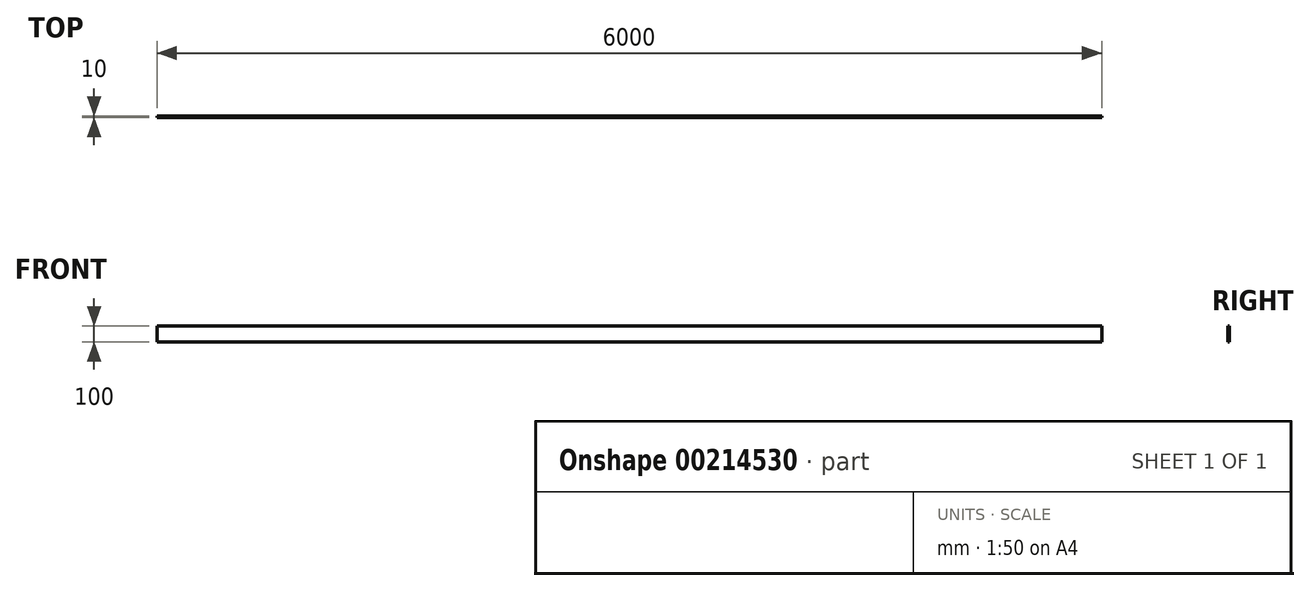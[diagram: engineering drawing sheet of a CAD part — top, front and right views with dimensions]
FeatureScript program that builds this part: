
annotation { "Feature Type Name" : "Feature", "Feature Type Description" : "" }
export const myFeature = defineFeature(function(context is Context, id is Id, definition is map)
    precondition{}
    {
        {
            var Q0;
            Q0=qCreatedBy(makeId("Front.planeOp"),FACE);
            var sketch = newSketch(context, id + "F0", { "sketchPlane" : qUnion([Q0])});
            skLineSegment(sketch, "E0.bottom", {"start": v(-3000, 50) * mm, "end": v(3000, 50) * mm});
            skLineSegment(sketch, "E0.top", {"start": v(-3000, -50) * mm, "end": v(3000, -50) * mm});
            skLineSegment(sketch, "E0.left", {"start": v(-3000, 50) * mm, "end": v(-3000, -50) * mm});
            skLineSegment(sketch, "E0.right", {"start": v(3000, 50) * mm, "end": v(3000, -50) * mm});
            skSolve(sketch);
        }
        {
            var Q0;
            Q0 = qSketchRegion(id + "F0", true);
            extrude(context, id + "F1", {"entities" : qUnion([Q0]), "depth" : 10 * mm});
        }
    });
